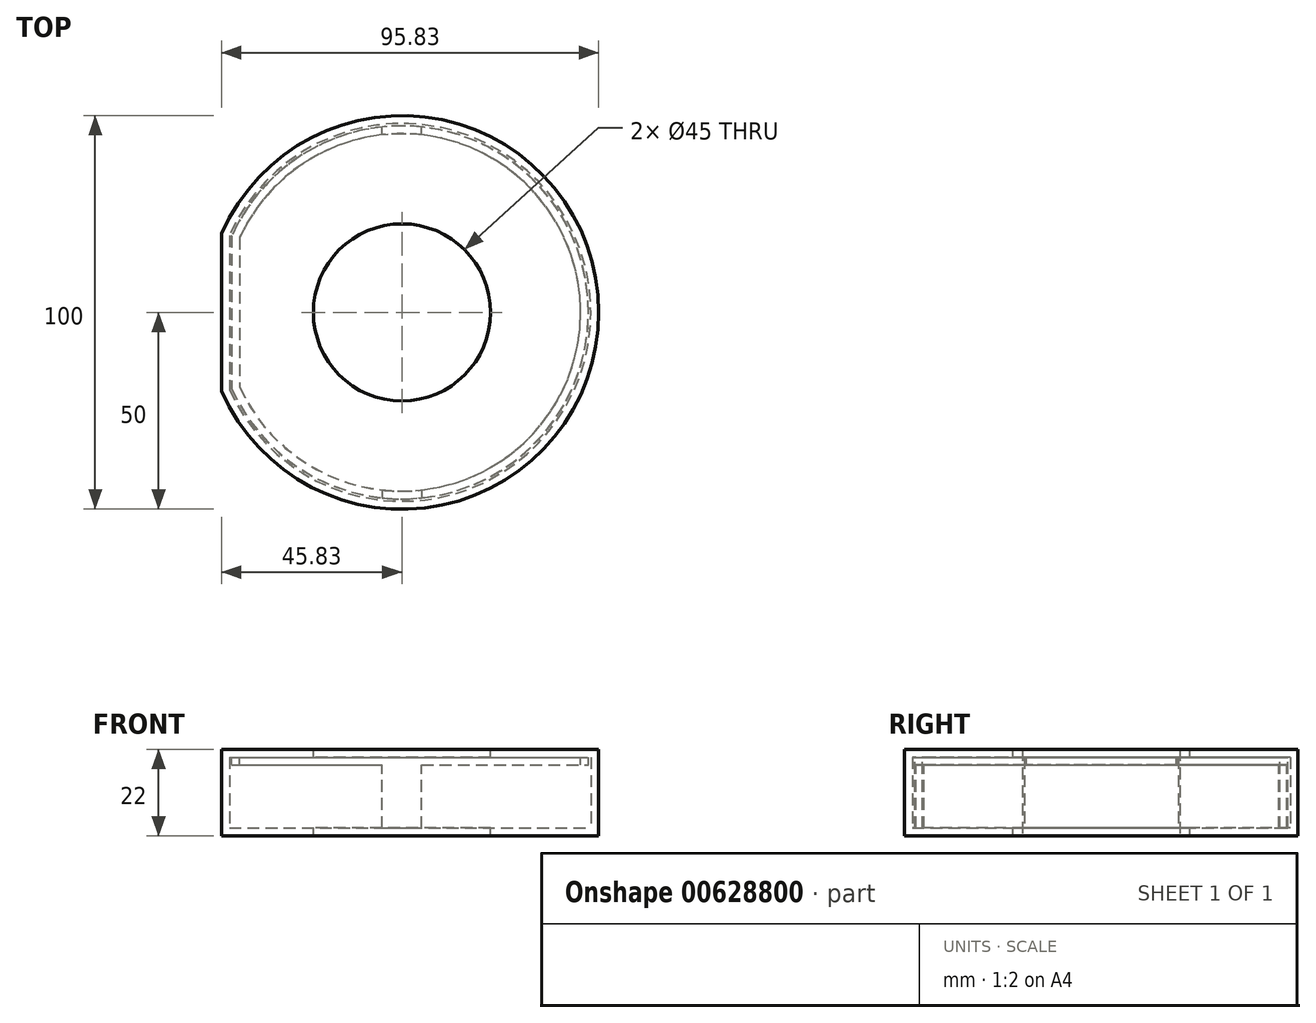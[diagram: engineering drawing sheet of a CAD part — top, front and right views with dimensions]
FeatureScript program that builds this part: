
annotation { "Feature Type Name" : "Feature", "Feature Type Description" : "" }
export const myFeature = defineFeature(function(context is Context, id is Id, definition is map)
    precondition{}
    {
        {
            var Q0;
            Q0=qCreatedBy(makeId("Top.planeOp"),FACE);
            var sketch = newSketch(context, id + "F0", { "sketchPlane" : qUnion([Q0])});
            skCircle(sketch, "E0", {"center": v(0, 0) * mm, "radius": 50 * mm});
            skCircle(sketch, "E1", {"center": v(0, 0) * mm, "radius": 15 * mm});
            skLineSegment(sketch, "E2", {"start": v(-45.83, 20) * mm, "end": v(-45.83, -20) * mm});
            skSolve(sketch);
        }
        {
            var Q0;
            Q0=makeQuery(id+"F0.imprint","IMPRINT",FACE,{"disambiguationData":[TD([[makeQuery(id+"F0.imprint","IMPRINT",EDGE,{"derivedFrom":sQuery(id+"F0.wireOp",EDGE,"E1")}),-1.0]])]});
            var Q1;
            Q1=makeQuery(id+"F0.imprint","IMPRINT",FACE,{"disambiguationData":[TD([[makeQuery(id+"F0.imprint","IMPRINT",EDGE,{"derivedFrom":sQuery(id+"F0.wireOp",EDGE,"E1")}),1.0]])]});
            extrude(context, id + "F1", {"entities" : qUnion([Q0, Q1]), "depth" : 20 * mm, "offsetDistance" : 25 * mm});
        }
        {
            var Q0;
            Q0=makeQuery(id+"F1.opExtrude","CAP_FACE",FACE,{"disambiguationData":[OSD([sQuery(id+"F0.wireOp",EDGE,"E0"),sQuery(id+"F0.wireOp",EDGE,"E2")])],"isStart":false});
            shell(context, id + "F2", {"entities" : qUnion([Q0]), "thickness" : 2 * mm});
        }
        {
            var Q0;
            Q0=makeQuery(id+"F1.opExtrude","CAP_FACE",FACE,{"disambiguationData":[OSD([sQuery(id+"F0.wireOp",EDGE,"E0"),sQuery(id+"F0.wireOp",EDGE,"E2")])],"isStart":false});
            var sketch = newSketch(context, id + "F3", { "sketchPlane" : qUnion([Q0])});
            skArc(sketch, "E3.0", {"start": v(-45.83, -20) * mm, "mid": v(50, 0) * mm, "end": v(-45.83, 20) * mm});
            skLineSegment(sketch, "E4.0", {"start": v(-45.83, 20) * mm, "end": v(-45.83, -20) * mm});
            skLineSegment(sketch, "E5.0", {"start": v(-43.83, 19.58) * mm, "end": v(-43.83, -19.58) * mm, "construction": true});
            skArc(sketch, "E6.0", {"start": v(-43.83, -19.58) * mm, "mid": v(48, 0) * mm, "end": v(-43.83, 19.58) * mm, "construction": true});
            skLineSegment(sketch, "E7.0", {"start": v(-43.23, 19.45) * mm, "end": v(-43.23, -19.45) * mm});
            skArc(sketch, "E7.1", {"start": v(-43.23, -19.45) * mm, "mid": v(47.4, 0) * mm, "end": v(-43.23, 19.45) * mm});
            skSolve(sketch);
        }
        {
            var Q0;
            Q0 = qSketchRegion(id + "F3", true);
            var Q1;
            Q1=makeQuery(id+"F3.imprint","IMPRINT",FACE,{"disambiguationData":[TD([[makeQuery(id+"F3.imprint","IMPRINT",EDGE,{"derivedFrom":sQuery(id+"F3.wireOp",EDGE,"E7.0")}),1.0]])]});
            extrude(context, id + "F4", {"entities" : qUnion([Q0, Q1]), "depth" : 2 * mm, "offsetDistance" : 25 * mm});
        }
        {
            var Q0;
            Q0=makeQuery(id+"F3.imprint","IMPRINT",FACE,{"disambiguationData":[TD([[makeQuery(id+"F3.imprint","IMPRINT",EDGE,{"derivedFrom":sQuery(id+"F3.wireOp",EDGE,"E7.0")}),1.0]])]});
            extrude(context, id + "F5", {"entities" : qUnion([Q0]), "operationType" : NewBodyOperationType.ADD, "oppositeDirection" : true, "depth" : 2 * mm, "offsetDistance" : 25 * mm});
        }
        {
            var Q0;
            Q0=makeQuery(id+"F5.opExtrude","CAP_FACE",FACE,{"disambiguationData":[OSD([sQuery(id+"F3.wireOp",EDGE,"E7.0"),sQuery(id+"F3.wireOp",EDGE,"E7.1")])],"isStart":false});
            shell(context, id + "F6", {"entities" : qUnion([Q0]), "thickness" : 2 * mm});
        }
        {
            var Q0;
            Q0=makeQuery(id+"F5.opExtrude","CAP_FACE",FACE,{"disambiguationData":[OSD([sQuery(id+"F3.wireOp",EDGE,"E7.0"),sQuery(id+"F3.wireOp",EDGE,"E7.1")])],"isStart":false});
            var sketch = newSketch(context, id + "F7", { "sketchPlane" : qUnion([Q0])});
            skLineSegment(sketch, "E8", {"start": v(0, 0) * mm, "end": v(-5, 0) * mm, "construction": true});
            skLineSegment(sketch, "E9", {"start": v(-5, -45.12) * mm, "end": v(-5, -47.14) * mm});
            skLineSegment(sketch, "E10", {"start": v(0, -45.4) * mm, "end": v(0, -47.4) * mm, "construction": true});
            skArc(sketch, "E11.0", {"start": v(0, -45.4) * mm, "mid": v(-2.5, -45.33) * mm, "end": v(-5, -45.12) * mm});
            skArc(sketch, "E12.0", {"start": v(0, -47.4) * mm, "mid": v(-2.5, -47.33) * mm, "end": v(-5, -47.14) * mm});
            skArc(sketch, "E13.MirrorCS", {"start": v(0, -47.4) * mm, "mid": v(2.5, -47.33) * mm, "end": v(5, -47.14) * mm});
            skArc(sketch, "E14.MirrorCS", {"start": v(0, -45.4) * mm, "mid": v(2.5, -45.33) * mm, "end": v(5, -45.12) * mm});
            skLineSegment(sketch, "E15.MirrorCS", {"start": v(5, -45.12) * mm, "end": v(5, -47.14) * mm});
            skLineSegment(sketch, "E16.MirrorCS", {"start": v(5, 45.12) * mm, "end": v(5, 47.14) * mm});
            skArc(sketch, "E17.MirrorCS", {"start": v(0, 47.4) * mm, "mid": v(2.5, 47.33) * mm, "end": v(5, 47.14) * mm});
            skArc(sketch, "E18.MirrorCS", {"start": v(0, 47.4) * mm, "mid": v(-2.5, 47.33) * mm, "end": v(-5, 47.14) * mm});
            skLineSegment(sketch, "E19.MirrorCS", {"start": v(-5, 45.12) * mm, "end": v(-5, 47.14) * mm});
            skArc(sketch, "E20.MirrorCS", {"start": v(0, 45.4) * mm, "mid": v(-2.5, 45.33) * mm, "end": v(-5, 45.12) * mm});
            skArc(sketch, "E21.MirrorCS", {"start": v(0, 45.4) * mm, "mid": v(2.5, 45.33) * mm, "end": v(5, 45.12) * mm});
            skSolve(sketch);
        }
        {
            var Q0;
            Q0 = qSketchRegion(id + "F7", true);
            extrude(context, id + "F8", {"entities" : qUnion([Q0]), "operationType" : NewBodyOperationType.ADD, "endBound" : BoundingType.UP_TO_NEXT, "depth" : 25 * mm, "offsetDistance" : 25 * mm});
        }
        {
            var Q0;
            Q0=makeQuery(id+"F4.opExtrude","CAP_FACE",FACE,{"disambiguationData":[OSD([sQuery(id+"F3.wireOp",EDGE,"E3.0"),sQuery(id+"F3.wireOp",EDGE,"E4.0")])],"isStart":false});
            var sketch = newSketch(context, id + "F9", { "sketchPlane" : qUnion([Q0])});
            skCircle(sketch, "E22", {"center": v(0, 0) * mm, "radius": 22.5 * mm});
            skSolve(sketch);
        }
        {
            var Q0;
            Q0=makeQuery(id+"F9.imprint","IMPRINT",FACE,{"disambiguationData":[TD([[makeQuery(id+"F9.imprint","IMPRINT",EDGE,{"derivedFrom":sQuery(id+"F9.wireOp",EDGE,"E22")}),1.0]])]});
            extrude(context, id + "F10", {"entities" : qUnion([Q0]), "operationType" : NewBodyOperationType.REMOVE, "oppositeDirection" : true, "depth" : 25 * mm, "offsetDistance" : 25 * mm});
        }
    });
